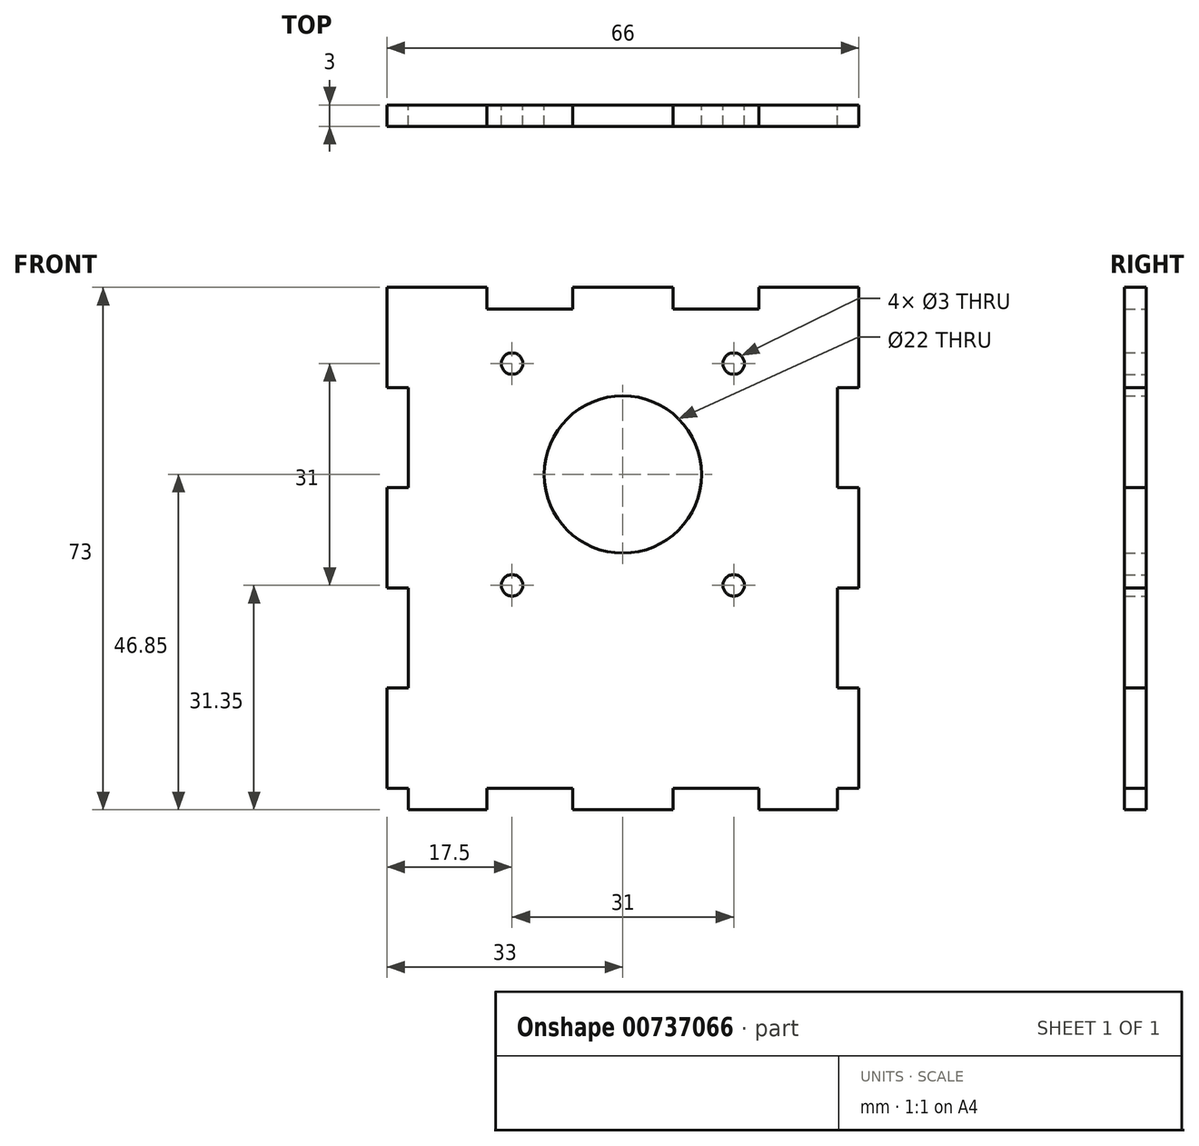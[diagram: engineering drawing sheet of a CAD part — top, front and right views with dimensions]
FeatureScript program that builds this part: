
annotation { "Feature Type Name" : "Feature", "Feature Type Description" : "" }
export const myFeature = defineFeature(function(context is Context, id is Id, definition is map)
    precondition{}
    {
        {
            var Q0;
            Q0=qCreatedBy(makeId("Front.planeOp"),FACE);
            var sketch = newSketch(context, id + "F0", { "sketchPlane" : qUnion([Q0])});
            skLineSegment(sketch, "E0.bottom", {"start": v(21.15, -21.15) * mm, "end": v(-21.15, -21.15) * mm, "construction": true});
            skLineSegment(sketch, "E0.top", {"start": v(21.15, 21.15) * mm, "end": v(-21.15, 21.15) * mm, "construction": true});
            skLineSegment(sketch, "E0.left", {"start": v(21.15, -21.15) * mm, "end": v(21.15, 21.15) * mm, "construction": true});
            skLineSegment(sketch, "E0.right", {"start": v(-21.15, -21.15) * mm, "end": v(-21.15, 21.15) * mm, "construction": true});
            skPoint(sketch, "E0.middle", {"position": v(0, 0) * mm});
            skCircle(sketch, "E1", {"center": v(0, 0) * mm, "radius": 11 * mm});
            skPoint(sketch, "E2", {"position": v(15.5, 15.5) * mm});
            skPoint(sketch, "E3", {"position": v(15.5, -15.5) * mm});
            skPoint(sketch, "E4", {"position": v(-15.5, -15.5) * mm});
            skPoint(sketch, "E5", {"position": v(-15.5, 15.5) * mm});
            skCircle(sketch, "E6", {"center": v(-15.5, 15.5) * mm, "radius": 1.5 * mm});
            skCircle(sketch, "E7", {"center": v(15.5, 15.5) * mm, "radius": 1.5 * mm});
            skCircle(sketch, "E8", {"center": v(15.5, -15.5) * mm, "radius": 1.5 * mm});
            skCircle(sketch, "E9", {"center": v(-15.5, -15.5) * mm, "radius": 1.5 * mm});
            skLineSegment(sketch, "E10", {"start": v(-33, 26.15) * mm, "end": v(-33, -43.85) * mm, "construction": true});
            skLineSegment(sketch, "E11", {"start": v(-33, -43.85) * mm, "end": v(33, -43.85) * mm, "construction": true});
            skLineSegment(sketch, "E12", {"start": v(33, -43.85) * mm, "end": v(33, 26.15) * mm, "construction": true});
            skLineSegment(sketch, "E13", {"start": v(33, 26.15) * mm, "end": v(-33, 26.15) * mm, "construction": true});
            skLineSegment(sketch, "E14", {"start": v(33, 12.15) * mm, "end": v(30, 12.15) * mm});
            skLineSegment(sketch, "E15", {"start": v(30, 12.15) * mm, "end": v(30, -1.85) * mm});
            skLineSegment(sketch, "E16", {"start": v(30, -1.85) * mm, "end": v(33, -1.85) * mm});
            skLineSegment(sketch, "E17", {"start": v(33, -1.85) * mm, "end": v(33, -15.85) * mm});
            skLineSegment(sketch, "E18", {"start": v(33, -15.85) * mm, "end": v(30, -15.85) * mm});
            skLineSegment(sketch, "E19", {"start": v(30, -15.85) * mm, "end": v(30, -29.85) * mm});
            skLineSegment(sketch, "E20", {"start": v(30, -29.85) * mm, "end": v(33, -29.85) * mm});
            skLineSegment(sketch, "E21", {"start": v(-33, 12.15) * mm, "end": v(-30, 12.15) * mm});
            skLineSegment(sketch, "E22", {"start": v(-30, 12.15) * mm, "end": v(-30, -1.85) * mm});
            skLineSegment(sketch, "E23", {"start": v(-30, -1.85) * mm, "end": v(-33, -1.85) * mm});
            skLineSegment(sketch, "E24", {"start": v(-33, -1.85) * mm, "end": v(-33, -15.85) * mm});
            skLineSegment(sketch, "E25", {"start": v(-33, -15.85) * mm, "end": v(-30, -15.85) * mm});
            skLineSegment(sketch, "E26", {"start": v(-30, -15.85) * mm, "end": v(-30, -29.85) * mm});
            skLineSegment(sketch, "E27", {"start": v(-30, -29.85) * mm, "end": v(-33, -29.85) * mm});
            skLineSegment(sketch, "E28", {"start": v(-19, 26.15) * mm, "end": v(-19, 23.15) * mm});
            skLineSegment(sketch, "E29", {"start": v(-19, 23.15) * mm, "end": v(-7, 23.15) * mm});
            skLineSegment(sketch, "E30", {"start": v(-7, 23.15) * mm, "end": v(-7, 26.15) * mm});
            skLineSegment(sketch, "E31", {"start": v(7, 26.15) * mm, "end": v(7, 23.15) * mm});
            skLineSegment(sketch, "E32", {"start": v(7, 23.15) * mm, "end": v(19, 23.15) * mm});
            skLineSegment(sketch, "E33", {"start": v(19, 23.15) * mm, "end": v(19, 26.15) * mm});
            skLineSegment(sketch, "E34", {"start": v(-7, 26.15) * mm, "end": v(7, 26.15) * mm});
            skLineSegment(sketch, "E35", {"start": v(-19, 26.15) * mm, "end": v(-33, 26.15) * mm});
            skLineSegment(sketch, "E36", {"start": v(-33, 12.15) * mm, "end": v(-33, 26.15) * mm});
            skLineSegment(sketch, "E37", {"start": v(-33, -29.85) * mm, "end": v(-33, -43.85) * mm});
            skLineSegment(sketch, "E38", {"start": v(33, -43.85) * mm, "end": v(33, -29.85) * mm});
            skLineSegment(sketch, "E39", {"start": v(33, 12.15) * mm, "end": v(33, 26.15) * mm});
            skLineSegment(sketch, "E40", {"start": v(33, 26.15) * mm, "end": v(19, 26.15) * mm});
            skLineSegment(sketch, "E41", {"start": v(-19, -46.85) * mm, "end": v(-19, -43.85) * mm});
            skLineSegment(sketch, "E42", {"start": v(-19, -43.85) * mm, "end": v(-7, -43.85) * mm});
            skLineSegment(sketch, "E43", {"start": v(-7, -43.85) * mm, "end": v(-7, -46.85) * mm});
            skLineSegment(sketch, "E44", {"start": v(-7, -46.85) * mm, "end": v(7, -46.85) * mm});
            skLineSegment(sketch, "E45", {"start": v(7, -46.85) * mm, "end": v(7, -43.85) * mm});
            skLineSegment(sketch, "E46", {"start": v(7, -43.85) * mm, "end": v(19, -43.85) * mm});
            skLineSegment(sketch, "E47", {"start": v(19, -43.85) * mm, "end": v(19, -46.85) * mm});
            skLineSegment(sketch, "E48", {"start": v(-19, -46.85) * mm, "end": v(-30, -46.85) * mm});
            skLineSegment(sketch, "E49", {"start": v(-30, -46.85) * mm, "end": v(-30, -43.85) * mm});
            skLineSegment(sketch, "E50", {"start": v(-30, -43.85) * mm, "end": v(-33, -43.85) * mm});
            skLineSegment(sketch, "E51", {"start": v(19, -46.85) * mm, "end": v(30, -46.85) * mm});
            skLineSegment(sketch, "E52", {"start": v(30, -46.85) * mm, "end": v(30, -43.85) * mm});
            skLineSegment(sketch, "E53", {"start": v(30, -43.85) * mm, "end": v(33, -43.85) * mm});
            skSolve(sketch);
        }
        {
            var Q0;
            Q0=makeQuery(id+"F0.imprint","IMPRINT",FACE,{"disambiguationData":[TD([[makeQuery(id+"F0.imprint","IMPRINT",EDGE,{"derivedFrom":sQuery(id+"F0.wireOp",EDGE,"E1")}),-1.0]])]});
            extrude(context, id + "F1", {"entities" : qUnion([Q0]), "depth" : 3 * mm, "offsetDistance" : 25 * mm});
        }
    });
